# Revit family: QF_Vulcan_VC44GD_Oven
name_source: partatom
category: Specialty Equipment
revit_build: Autodesk Revit 2017 (Build: 20181011_1645(x64)
units: mm (PartAtom-declared; Revit-internal decimal feet)

## family parameters
Always vertical = Yes
Cut with Voids When Loaded = No
OmniClass Number = 23.40.40.14.17.11
OmniClass Title = Cookers, Ovens, Stoves
Part Type = Normal
Room Calculation Point = No
Round Connector Dimension = Use Radius
Shared = No
Work Plane-Based = No

## types (1)
- VC44GD
    Apparent Power = 960 VA
    Assembly Code = E1090320
    Black Metal = Metal - Black Enamel
    Black Plastic = Plastic - Black
    CSI MasterFormat = 11 44 16
    Chrome = Metal - Chrome
    Clearance = Clearances
    Computer Controls = Yes
    Conn Plug = NEMA 5-15P
    Conn Plug NEMA = 5-15P
    Cycle = 60 Hz
    Description = Double-Deck Convection Oven
    Elec Conn Connection Height = 1' - 5"
    Electric Connection Type = (2) Cord & Plug
    FL Amps = 8 A
    Gas Connection Height = 1' - 2 1/2"
    Gas Input = 50000.0 Btu/h
    Gas KW = 25.8
    Gas Radius = 0"
    Gas Size = 1"
    Glass = Glass
    HP = 1/2
    KCL SpecSheet URL = http://kclweb.kclcad.com
    KCLRef = KCL2C9,,00032efa-0000-0000-0000-000000000307,VH,VC44GD ,634700225660000000,4fdffdde-5a5f-412c-ba2a-7357cdfce0d7,7ebc4af2-1ef8-45b1-a82a-850d0d805eba
    Leg Material = Metal - Black Enamel
    Manufacturer = Vulcan-Hart
    Model = VC44GD
    Number of Poles = 1
    Phase = 1
    Red Plastic = Plastic - Red
    Solid State Controls = Yes
    Stainless Steel = Metal - Stainless Steel
    Type Comments = Solid State Controls
    URL = https://my.vulcanfeg.com
    URL Cutsheet = https://my.vulcanfeg.com
    URL Manufacturer = www.vulcanequipment.com
    Volts = 120 V
    Weight = 994

## geometry (parser evidence)
native form markers: Blend x18, Sweep x7
no freeform markers — native parametric forms only
